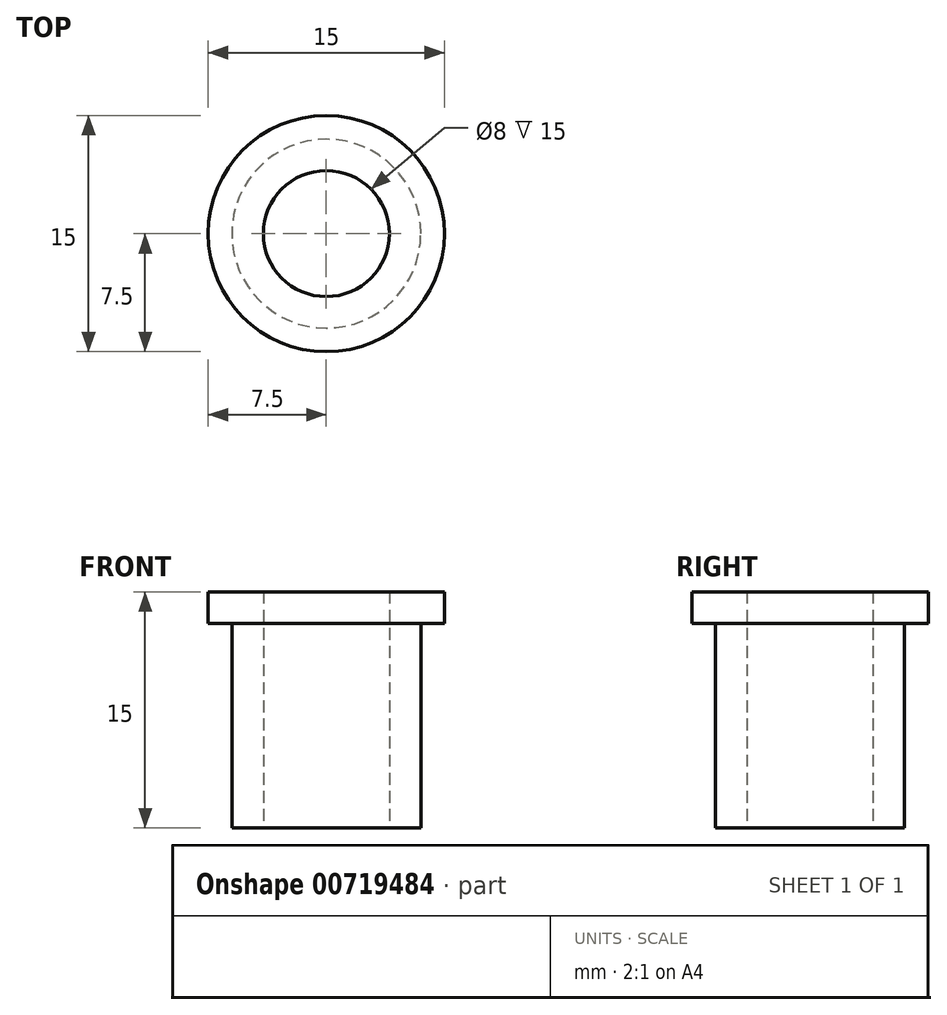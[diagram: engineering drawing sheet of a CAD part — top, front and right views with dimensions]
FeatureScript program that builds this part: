
annotation { "Feature Type Name" : "Feature", "Feature Type Description" : "" }
export const myFeature = defineFeature(function(context is Context, id is Id, definition is map)
    precondition{}
    {
        {
            var Q0;
            Q0=qCreatedBy(makeId("Front.planeOp"),FACE);
            var sketch = newSketch(context, id + "F0", { "sketchPlane" : qUnion([Q0])});
            skLineSegment(sketch, "E0", {"start": v(-4, 15) * mm, "end": v(-4, 0) * mm});
            skLineSegment(sketch, "E1", {"start": v(-4, 0) * mm, "end": v(-6, 0) * mm});
            skLineSegment(sketch, "E2", {"start": v(-6, 0) * mm, "end": v(-6, 13) * mm});
            skLineSegment(sketch, "E3", {"start": v(-6, 13) * mm, "end": v(-7.5, 13) * mm});
            skLineSegment(sketch, "E4", {"start": v(-7.5, 13) * mm, "end": v(-7.5, 15) * mm});
            skLineSegment(sketch, "E5", {"start": v(-7.5, 15) * mm, "end": v(-4, 15) * mm});
            skLineSegment(sketch, "E6", {"start": v(0, 0) * mm, "end": v(0, 12.67) * mm, "construction": true});
            skSolve(sketch);
        }
        {
            var Q0;
            Q0=makeQuery(id+"F0.imprint","IMPRINT",FACE,{"disambiguationData":[TD([[makeQuery(id+"F0.imprint","IMPRINT",EDGE,{"derivedFrom":sQuery(id+"F0.wireOp",EDGE,"E0")}),-1.0]])]});
            var Q1;
            Q1=sQuery(id+"F0.wireOp",EDGE,"E6");
            revolve(context, id + "F1", {"surfaceOperationType" : NewSurfaceOperationType.NEW, "entities" : qUnion([Q0]), "axis" : qUnion([Q1]), "revolveType" : RevolveType.FULL});
        }
    });
